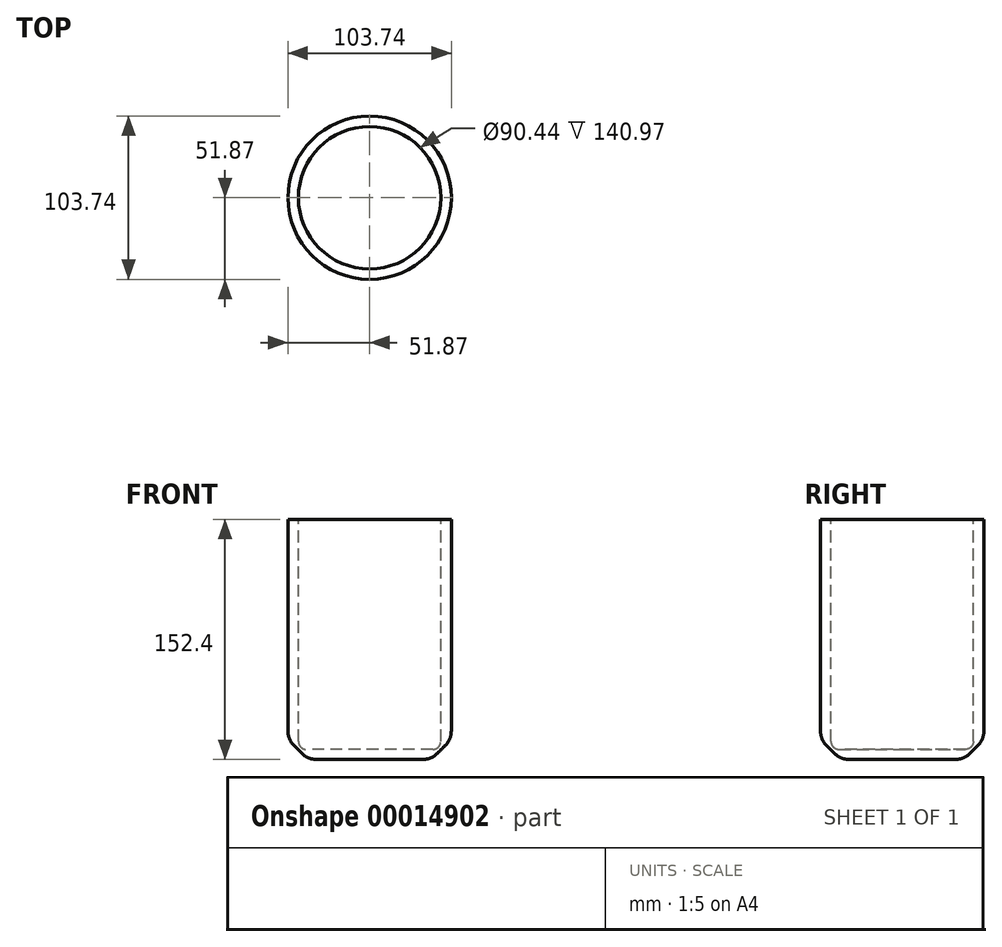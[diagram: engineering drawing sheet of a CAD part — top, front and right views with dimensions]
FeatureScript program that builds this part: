
annotation { "Feature Type Name" : "Feature", "Feature Type Description" : "" }
export const myFeature = defineFeature(function(context is Context, id is Id, definition is map)
    precondition{}
    {
        {
            var Q0;
            Q0=qCreatedBy(makeId("Top.planeOp"),FACE);
            var sketch = newSketch(context, id + "F0", { "sketchPlane" : qUnion([Q0])});
            skCircle(sketch, "E0", {"center": v(0, 0) * mm, "radius": 51.87 * mm});
            skSolve(sketch);
        }
        {
            var Q0;
            Q0=makeQuery(id+"F0.imprint","IMPRINT",FACE,{"disambiguationData":[TD([[makeQuery(id+"F0.imprint","IMPRINT",EDGE,{"derivedFrom":sQuery(id+"F0.wireOp",EDGE,"E0")}),1.0]])]});
            extrude(context, id + "F1", {"entities" : qUnion([Q0]), "depth" : 152.4 * mm});
        }
        {
            var Q0;
            Q0=makeQuery(id+"F1.opExtrude","CAP_FACE",FACE,{"disambiguationData":[OSD([sQuery(id+"F0.wireOp",EDGE,"E0")])],"isStart":false});
            var sketch = newSketch(context, id + "F2", { "sketchPlane" : qUnion([Q0])});
            skCircle(sketch, "E1", {"center": v(0, 0) * mm, "radius": 45.22 * mm});
            skSolve(sketch);
        }
        {
            var Q0;
            Q0=makeQuery(id+"F2.imprint","IMPRINT",FACE,{"disambiguationData":[TD([[makeQuery(id+"F2.imprint","IMPRINT",EDGE,{"derivedFrom":sQuery(id+"F2.wireOp",EDGE,"E1")}),1.0]])]});
            extrude(context, id + "F3", {"entities" : qUnion([Q0]), "operationType" : NewBodyOperationType.REMOVE, "oppositeDirection" : true, "depth" : 146.05 * mm});
        }
        {
            var Q0;
            Q0=makeQuery(id+"F1.opExtrude","CAP_EDGE",EDGE,{"disambiguationData":[OSD([sQuery(id+"F0.wireOp",EDGE,"E0")])],"isStart":true});
            chamfer(context, id + "F4", {"entities" : qUnion([Q0]), "width" : 12.7 * mm, "tangentPropagation" : true});
        }
        {
            var Q0;
            Q0=makeQuery(id+"F3.boolean.opBoolean","COPY",EDGE,{"derivedFrom":makeQuery(id+"F3.opExtrude","CAP_EDGE",EDGE,{"disambiguationData":[OSD([sQuery(id+"F2.wireOp",EDGE,"E1")])],"isStart":false})});
            fillet(context, id + "F5", {"entities" : qUnion([Q0]), "radius" : 5.08 * mm, "tangentPropagation" : true, "allowEdgeOverflow" : false});
        }
        {
            var Q0;
            {var subQ0=sQuery(id+"F0.wireOp",EDGE,"E0");Q0=makeQuery(id+"F4.opChamfer","BLEND_EDGE",EDGE,{"blendedFrom":[makeQuery(id+"F1.opExtrude","CAP_EDGE",EDGE,{"disambiguationData":[OSD([subQ0])],"isStart":true}),makeQuery(id+"F1.opExtrude","SWEPT_FACE",FACE,{"disambiguationData":[OSD([subQ0])]})],"blendedInto":[makeQuery(id+"F1.opExtrude","SWEPT_FACE",FACE,{"disambiguationData":[OSD([subQ0])]})]});}
            var Q1;
            {var subQ0=sQuery(id+"F0.wireOp",EDGE,"E0");Q1=makeQuery(id+"F4.opChamfer","BLEND_EDGE",EDGE,{"blendedFrom":[makeQuery(id+"F1.opExtrude","CAP_EDGE",EDGE,{"disambiguationData":[OSD([subQ0])],"isStart":true}),makeQuery(id+"F1.opExtrude","CAP_FACE",FACE,{"disambiguationData":[OSD([subQ0])],"isStart":true})],"blendedInto":[makeQuery(id+"F1.opExtrude","CAP_FACE",FACE,{"disambiguationData":[OSD([subQ0])],"isStart":true})]});}
            fillet(context, id + "F6", {"entities" : qUnion([Q0, Q1]), "radius" : 12.7 * mm, "tangentPropagation" : true, "allowEdgeOverflow" : false});
        }
    });
